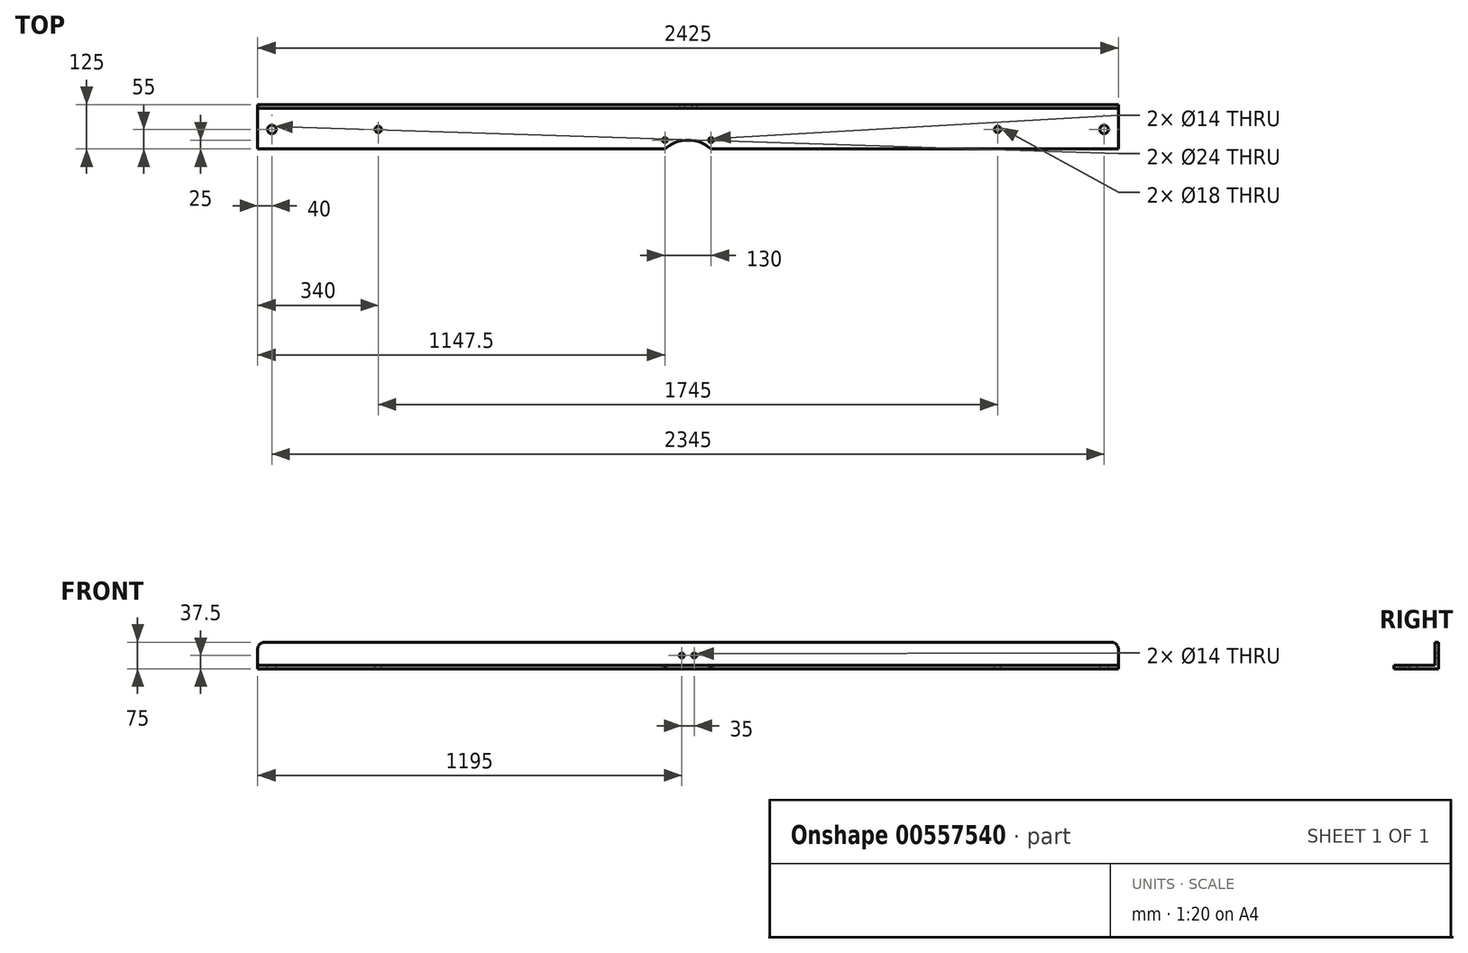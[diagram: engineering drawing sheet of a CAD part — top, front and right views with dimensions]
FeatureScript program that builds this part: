
annotation { "Feature Type Name" : "Feature", "Feature Type Description" : "" }
export const myFeature = defineFeature(function(context is Context, id is Id, definition is map)
    precondition{}
    {
        {
            var Q0;
            Q0=qCreatedBy(makeId("Right.planeOp"),FACE);
            var sketch = newSketch(context, id + "F0", { "sketchPlane" : qUnion([Q0])});
            skLineSegment(sketch, "E0", {"start": v(0, 0) * mm, "end": v(-125, 0) * mm});
            skLineSegment(sketch, "E1", {"start": v(-125, 0) * mm, "end": v(-125, 10) * mm});
            skLineSegment(sketch, "E2", {"start": v(-125, 10) * mm, "end": v(-10, 10) * mm});
            skLineSegment(sketch, "E3", {"start": v(-10, 10) * mm, "end": v(-10, 75) * mm});
            skLineSegment(sketch, "E4", {"start": v(-10, 75) * mm, "end": v(0, 75) * mm});
            skLineSegment(sketch, "E5", {"start": v(0, 75) * mm, "end": v(0, 0) * mm});
            skSolve(sketch);
        }
        {
            var Q0;
            Q0 = qSketchRegion(id + "F0", true);
            extrude(context, id + "F1", {"entities" : qUnion([Q0]), "flatOperationType" : FlatOperationType.REMOVE, "depth" : 2425 * mm, "offsetDistance" : 25 * mm, "domain" : OperationDomain.MODEL});
        }
        {
            var Q0;
            Q0=makeQuery(id+"F1.opExtrude","SWEPT_FACE",FACE,{"disambiguationData":[OSD([sQuery(id+"F0.wireOp",EDGE,"E2")])]});
            var sketch = newSketch(context, id + "F2", { "sketchPlane" : qUnion([Q0])});
            skCircle(sketch, "E6", {"center": v(40, -70) * mm, "radius": 12 * mm});
            skCircle(sketch, "E7", {"center": v(2385, -70) * mm, "radius": 12 * mm});
            skArc(sketch, "E8", {"start": v(1277.5, -125) * mm, "mid": v(1212.5, -100) * mm, "end": v(1147.5, -125) * mm});
            skCircle(sketch, "E9", {"center": v(1147.5, -100) * mm, "radius": 7 * mm});
            skCircle(sketch, "E10", {"center": v(1277.5, -100) * mm, "radius": 7 * mm});
            skLineSegment(sketch, "E11", {"start": v(1147.5, -125) * mm, "end": v(1277.5, -125) * mm});
            skCircle(sketch, "E12", {"center": v(2085, -70) * mm, "radius": 9 * mm});
            skCircle(sketch, "E13", {"center": v(340, -70) * mm, "radius": 9 * mm});
            skSolve(sketch);
        }
        {
            var Q0;
            Q0 = qSketchRegion(id + "F2", true);
            extrude(context, id + "F3", {"entities" : qUnion([Q0]), "operationType" : NewBodyOperationType.REMOVE, "flatOperationType" : FlatOperationType.REMOVE, "oppositeDirection" : true, "depth" : 10 * mm, "offsetDistance" : 25 * mm, "domain" : OperationDomain.MODEL});
        }
        {
            var Q0;
            Q0=makeQuery(id+"F1.opExtrude","SWEPT_FACE",FACE,{"disambiguationData":[OSD([sQuery(id+"F0.wireOp",EDGE,"E3")])]});
            var sketch = newSketch(context, id + "F4", { "sketchPlane" : qUnion([Q0])});
            skCircle(sketch, "E14", {"center": v(1195, 37.5) * mm, "radius": 7 * mm});
            skCircle(sketch, "E15", {"center": v(1230, 37.5) * mm, "radius": 7 * mm});
            skSolve(sketch);
        }
        {
            var Q0;
            Q0 = qSketchRegion(id + "F4", true);
            extrude(context, id + "F5", {"entities" : qUnion([Q0]), "operationType" : NewBodyOperationType.REMOVE, "flatOperationType" : FlatOperationType.REMOVE, "oppositeDirection" : true, "depth" : 10 * mm, "offsetDistance" : 25 * mm, "domain" : OperationDomain.MODEL});
        }
        {
            var Q0;
            Q0=makeQuery(id+"F1.opExtrude","CAP_EDGE",EDGE,{"disambiguationData":[OSD([sQuery(id+"F0.wireOp",EDGE,"E4")])],"isStart":false});
            var Q1;
            Q1=makeQuery(id+"F1.opExtrude","CAP_EDGE",EDGE,{"disambiguationData":[OSD([sQuery(id+"F0.wireOp",EDGE,"E4")])],"isStart":true});
            fillet(context, id + "F6", {"entities" : qUnion([Q0, Q1]), "radius" : 20 * mm, "tangentPropagation" : true, "defaultsChanged" : false, "allowEdgeOverflow" : false, "vertexSettings" : [], "filletType" : FilletType.EDGE});
        }
    });
